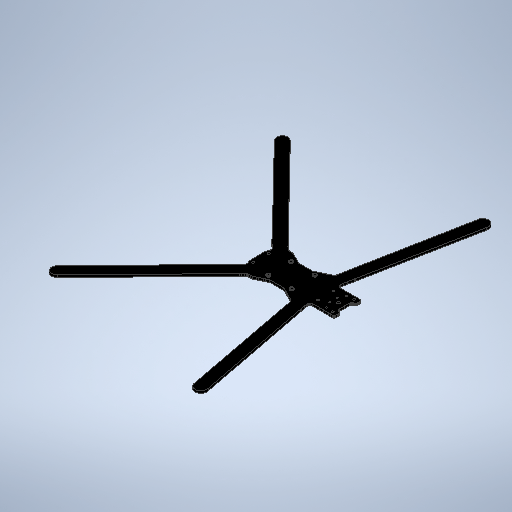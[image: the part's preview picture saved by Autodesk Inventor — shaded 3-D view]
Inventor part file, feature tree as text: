
AUTODESK INVENTOR PART (.ipt)
format: ipt  version: 2025.2 (Build 292293000, 293)  size: 2,962,432 bytes
history: native  units: in
note: dims shown in document units (in); Inventor stores cm internally (conversion verified against a paired STEP export)
features: extrude x20, sketch x20
ambient origin geometry x8: Origin, YZ Plane, XZ Plane, XY Plane, X Axis, Y Axis, Z Axis, Center Point
bodies: Solid1 (feature_tree)
feature tree (40):
  extrude  "Extrusion1"  Depth=0.1181in
  extrude  "Extrusion2"  Depth=0.1181in
  extrude  "Extrusion3"  Depth=0.126in
  extrude  "Extrusion4"  Depth=1.2008in
  extrude  "Extrusion5"  Depth=1.2008in
  extrude  "Extrusion6"  Depth=0.6004in
  extrude  "Extrusion7"  TaperAngle=90.0deg  [1 undecoded]
  extrude  "Extrusion8"  Depth=0.6004in
  extrude  "Extrusion9"  Depth=0.1181in TaperAngle=0.0deg
  extrude  "Extrusion10"  Depth=0.1181in
  extrude  "Extrusion11"  Depth=0.1181in TaperAngle=0.0deg
  extrude  "Extrusion12"  Depth=0.1181in
  extrude  "Extrusion13"  Depth=0.1969in
  extrude  "Extrusion14"  Depth=0.1181in TaperAngle=0.0deg
  extrude  "Extrusion15"  Depth=0.151in
  extrude  "Extrusion16"  Depth=0.1181in
  extrude  "Extrusion22"  Depth=0.1181in
  extrude  "Extrusion24"  Depth=0.1181in
  extrude  "Extrusion25"  Depth=0.3937in
  extrude  "Extrusion26"  Depth=0.0197in
  sketch  "Sketch1"  dims[d0=0.1181in d1=0.0in d2=5.1217in]
  sketch  "Sketch2"  dims[d3=0.1181in d4=0.0in d5=0.126in]
  sketch  "Sketch3"  dims[d6=0.126in d7=0.126in]
  sketch  "Sketch4"  dims[d8=0.126in d9=1.2008in]
  sketch  "Sketch5"  dims[d10=1.2008in d11=1.2008in]
  sketch  "Sketch6"  dims[d12=1.2008in d13=0.6004in]
  sketch  "Sketch7"  dims[d14=0.6004in d17=90.0deg]
  sketch  "Sketch8"  dims[d18=0.6004in d19=0.6004in]
  sketch  "Sketch9"  dims[d20=0.6004in d21=0.1181in d22=0.0in]
  sketch  "Sketch10"  dims[d23=0.1181in d24=0.1181in]
  sketch  "Sketch11"  dims[d25=0.1181in d26=0.1181in d27=0.0in]
  sketch  "Sketch12"  dims[d29=0.1181in d30=0.0in d31=0.1181in]
  sketch  "Sketch13"  dims[d32=0.1969in d33=0.1969in]
  sketch  "Sketch14"  dims[d34=0.1181in d35=0.0in d36=0.1181in d37=0.0in]
  sketch  "Sketch15"  dims[d38=0.1554in d39=0.151in]
  sketch  "Sketch17"  dims[d40=0.1181in d41=0.0in d42=0.1181in]
  sketch  "Sketch23"  dims[d43=0.1181in d44=0.1181in]
  sketch  "Sketch25"  dims[d45=0.1181in d46=0.5512in]
  sketch  "Sketch26"  dims[d47=0.5512in d48=0.3937in]
  sketch  "Sketch27"  dims[d49=0.3937in d50=0.9013in d51=0.1181in d52=0.0in d53=0.1181in d54=0.0in d55=0.1575in d56=0.1181in d57=0.0in d58=0.1181in d59=0.0in d60=0.0827in d61=0.1969in d62=0.5512in d63=0.0827in d64=0.315in d65=0.1575in d66=0.1181in d67=0.0in d68=0.1969in d69=0.1969in d70=0.1969in d71=0.1969in d72=0.0394in d73=0.0in d74=0.7874in d75=0.4528in d76=1.5748in d77=0.9055in d78=0.0197in d79=0.0in d80=0.0787in d81=0.0787in d82=0.0591in d83=0.0in d100=0.0197in d101=0.0in d114=0.1181in d115=0.0in d116=0.1181in d117=0.0in d118=0.1181in d119=0.0in d90=0.0197in d91=0.0344in d92=0.0197in d93=0.0344in]
note: 1 required parameter value undecoded (feature->parameter linkage not recoverable at this tier; creation-order binding heuristic only, values carry confidence <= 0.55)
